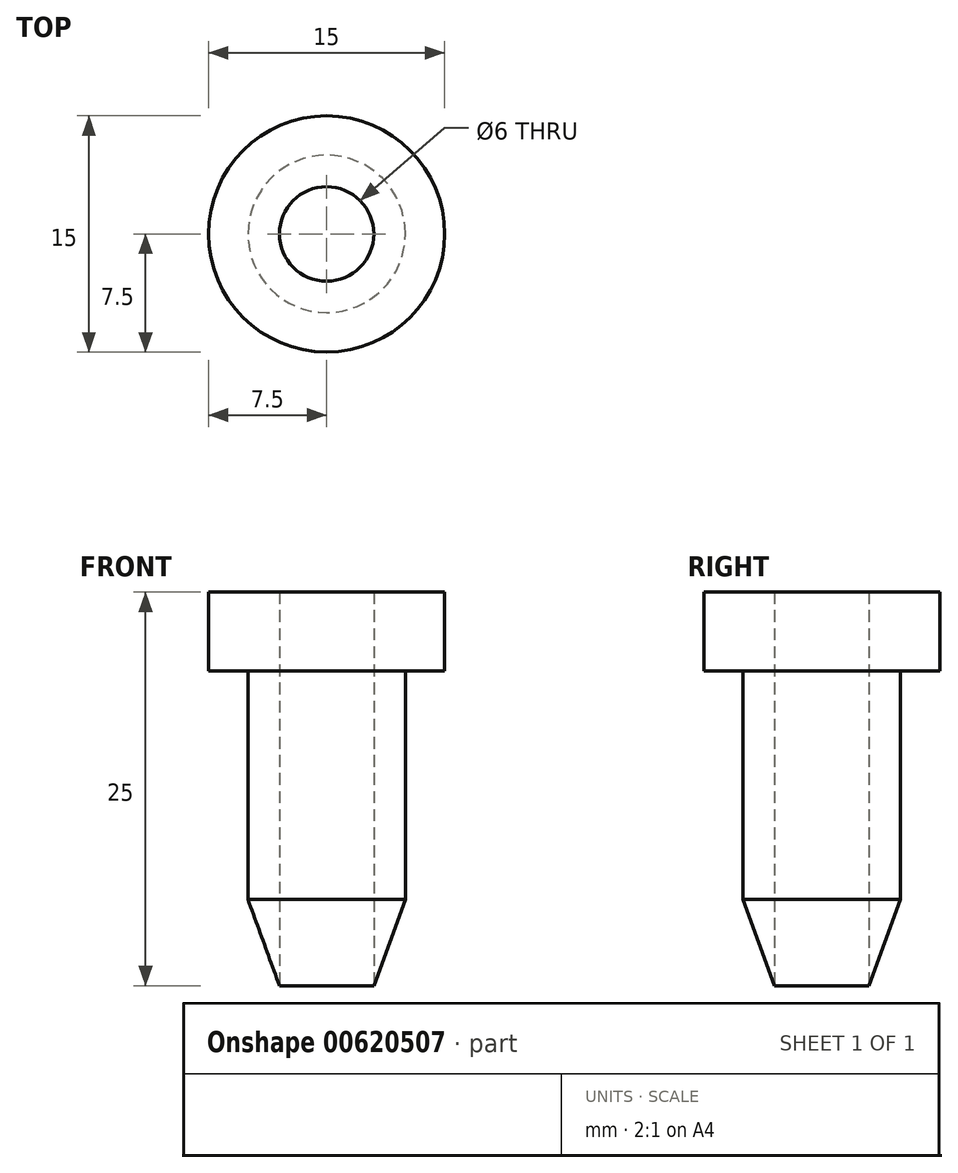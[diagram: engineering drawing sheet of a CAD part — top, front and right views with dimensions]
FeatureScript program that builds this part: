
annotation { "Feature Type Name" : "Feature", "Feature Type Description" : "" }
export const myFeature = defineFeature(function(context is Context, id is Id, definition is map)
    precondition{}
    {
        {
            var Q0;
            Q0=qCreatedBy(makeId("Front.planeOp"),FACE);
            var sketch = newSketch(context, id + "F0", { "sketchPlane" : qUnion([Q0])});
            skLineSegment(sketch, "E0", {"start": v(-3, 0) * mm, "end": v(-3, 25) * mm});
            skLineSegment(sketch, "E1", {"start": v(-3, 25) * mm, "end": v(-7.5, 25) * mm});
            skLineSegment(sketch, "E2", {"start": v(-7.5, 25) * mm, "end": v(-7.5, 20) * mm});
            skLineSegment(sketch, "E3", {"start": v(-7.5, 20) * mm, "end": v(-5, 20) * mm});
            skLineSegment(sketch, "E4", {"start": v(-5, 20) * mm, "end": v(-5, 5.5) * mm});
            skLineSegment(sketch, "E5", {"start": v(-5, 5.5) * mm, "end": v(-3, 0) * mm});
            skLineSegment(sketch, "E6", {"start": v(0, 0) * mm, "end": v(0, 32.13) * mm, "construction": true});
            skSolve(sketch);
        }
        {
            var Q0;
            Q0=makeQuery(id+"F0.imprint","IMPRINT",FACE,{"disambiguationData":[TD([[makeQuery(id+"F0.imprint","IMPRINT",EDGE,{"derivedFrom":sQuery(id+"F0.wireOp",EDGE,"E0")}),1.0]])]});
            var Q1;
            Q1=sQuery(id+"F0.wireOp",EDGE,"E6");
            revolve(context, id + "F1", {"entities" : qUnion([Q0]), "axis" : qUnion([Q1]), "revolveType" : RevolveType.FULL});
        }
    });
